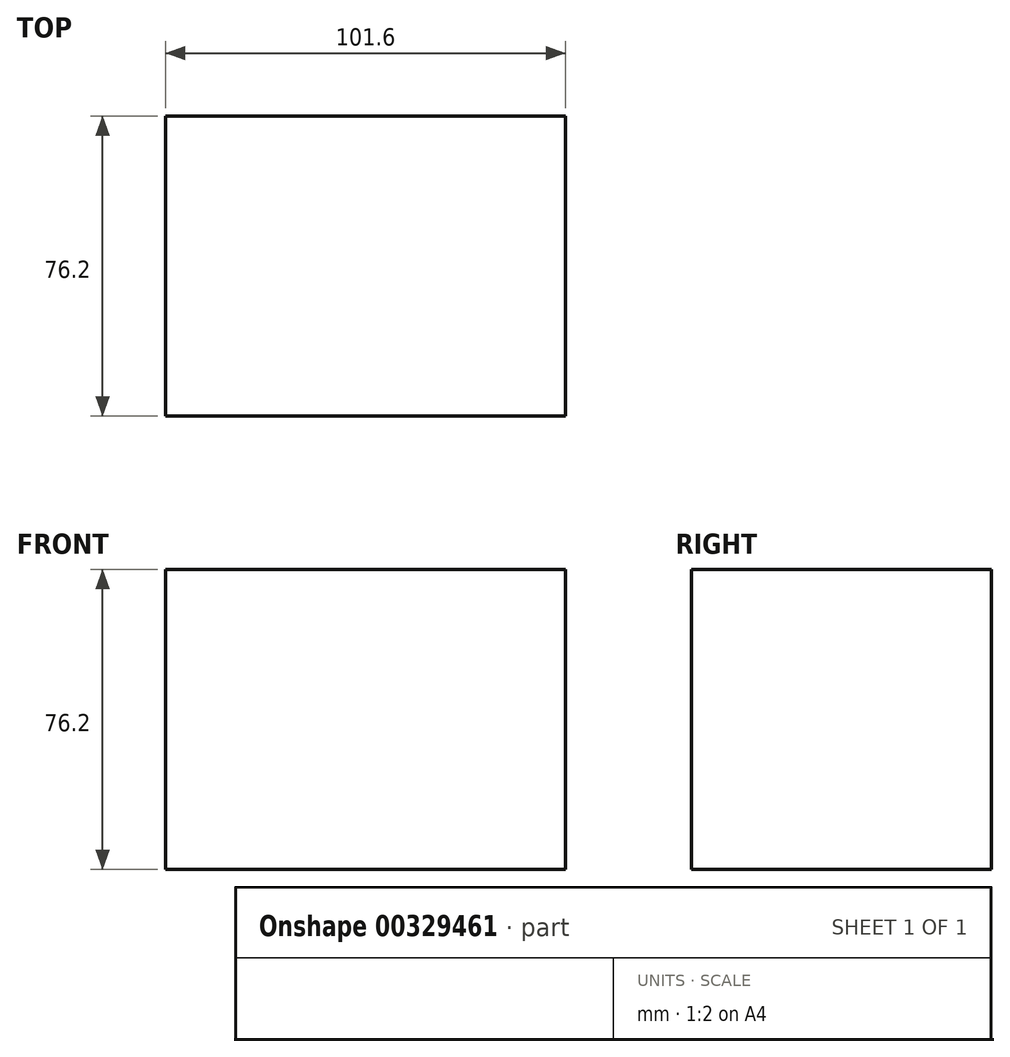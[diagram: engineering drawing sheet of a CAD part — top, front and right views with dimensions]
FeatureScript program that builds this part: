
annotation { "Feature Type Name" : "Feature", "Feature Type Description" : "" }
export const myFeature = defineFeature(function(context is Context, id is Id, definition is map)
    precondition{}
    {
        {
            var Q0;
            Q0=qCreatedBy(makeId("Top.planeOp"),FACE);
            var sketch = newSketch(context, id + "F0", { "sketchPlane" : qUnion([Q0])});
            skLineSegment(sketch, "E0.bottom", {"start": v(50.8, 38.1) * mm, "end": v(-50.8, 38.1) * mm});
            skLineSegment(sketch, "E0.top", {"start": v(50.8, -38.1) * mm, "end": v(-50.8, -38.1) * mm});
            skLineSegment(sketch, "E0.left", {"start": v(50.8, 38.1) * mm, "end": v(50.8, -38.1) * mm});
            skLineSegment(sketch, "E0.right", {"start": v(-50.8, 38.1) * mm, "end": v(-50.8, -38.1) * mm});
            skPoint(sketch, "E0.middle", {"position": v(0, 0) * mm});
            skSolve(sketch);
        }
        {
            var Q0;
            Q0 = qSketchRegion(id + "F0", true);
            extrude(context, id + "F1", {"entities" : qUnion([Q0]), "depth" : 76.2 * mm});
        }
    });
